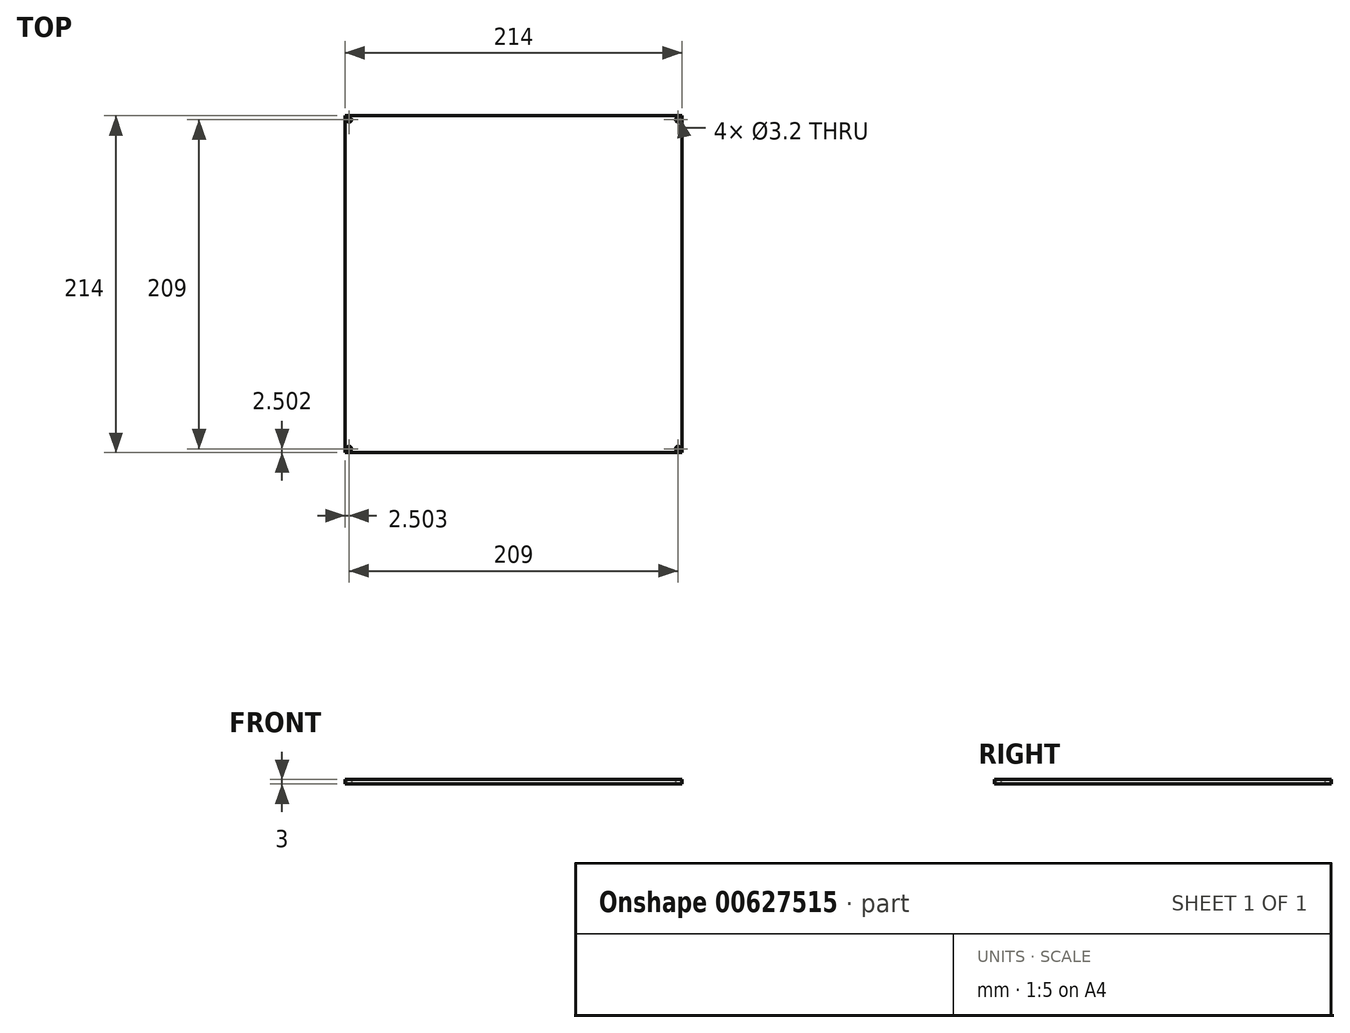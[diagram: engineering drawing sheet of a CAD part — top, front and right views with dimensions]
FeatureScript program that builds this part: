
annotation { "Feature Type Name" : "Feature", "Feature Type Description" : "" }
export const myFeature = defineFeature(function(context is Context, id is Id, definition is map)
    precondition{}
    {
        {
            var Q0;
            Q0=qCreatedBy(makeId("Top.planeOp"),FACE);
            var sketch = newSketch(context, id + "F0", { "sketchPlane" : qUnion([Q0])});
            skLineSegment(sketch, "E0.bottom", {"start": v(-107.16, 111.55) * mm, "end": v(106.84, 111.55) * mm});
            skLineSegment(sketch, "E0.top", {"start": v(-107.16, -102.45) * mm, "end": v(106.84, -102.45) * mm});
            skLineSegment(sketch, "E0.left", {"start": v(-107.16, 111.55) * mm, "end": v(-107.16, -102.45) * mm});
            skLineSegment(sketch, "E0.right", {"start": v(106.84, 111.55) * mm, "end": v(106.84, -102.45) * mm});
            skLineSegment(sketch, "E1.0", {"start": v(104.34, 109.05) * mm, "end": v(104.34, -99.95) * mm, "construction": true});
            skLineSegment(sketch, "E1.1", {"start": v(-104.66, 109.05) * mm, "end": v(104.34, 109.05) * mm, "construction": true});
            skLineSegment(sketch, "E1.2", {"start": v(-104.66, 109.05) * mm, "end": v(-104.66, -99.95) * mm, "construction": true});
            skLineSegment(sketch, "E1.3", {"start": v(-104.66, -99.95) * mm, "end": v(104.34, -99.95) * mm, "construction": true});
            skCircle(sketch, "E2", {"center": v(-104.66, 109.05) * mm, "radius": 2.5 * mm, "construction": true});
            skCircle(sketch, "E3", {"center": v(-104.66, -99.95) * mm, "radius": 2.5 * mm, "construction": true});
            skCircle(sketch, "E4", {"center": v(104.34, -99.95) * mm, "radius": 2.5 * mm, "construction": true});
            skCircle(sketch, "E5", {"center": v(104.34, 109.05) * mm, "radius": 2.5 * mm, "construction": true});
            skCircle(sketch, "E6.0", {"center": v(104.34, 109.05) * mm, "radius": 1.6 * mm});
            skCircle(sketch, "E7.0", {"center": v(-104.66, 109.05) * mm, "radius": 1.6 * mm});
            skCircle(sketch, "E8.0", {"center": v(-104.66, -99.95) * mm, "radius": 1.6 * mm});
            skCircle(sketch, "E9.0", {"center": v(104.34, -99.95) * mm, "radius": 1.6 * mm});
            skSolve(sketch);
        }
        {
            var Q0;
            Q0=makeQuery(id+"F0.imprint","IMPRINT",FACE,{"disambiguationData":[TD([[makeQuery(id+"F0.imprint","IMPRINT",EDGE,{"derivedFrom":sQuery(id+"F0.wireOp",EDGE,"E0.bottom")}),-1.0]])]});
            extrude(context, id + "F1", {"entities" : qUnion([Q0]), "depth" : 3 * mm, "offsetDistance" : 25 * mm});
        }
    });
